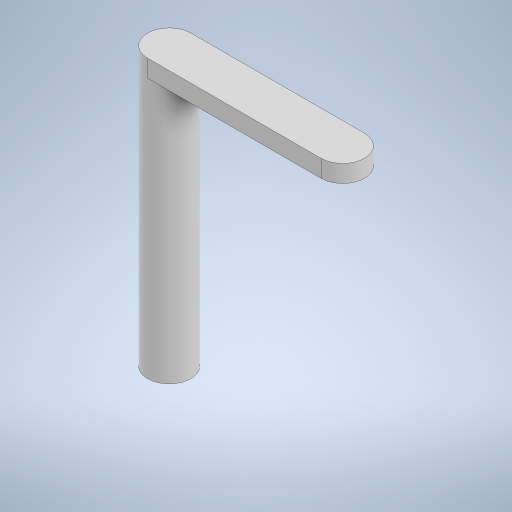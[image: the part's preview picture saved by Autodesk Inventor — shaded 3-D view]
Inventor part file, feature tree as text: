
AUTODESK INVENTOR PART (.ipt)
format: ipt  version: 2024 (Build 280153000, 153)  size: 237,568 bytes
history: native  units: in
note: dims shown in document units (in); Inventor stores cm internally (conversion verified against a paired STEP export)
features: extrude x2, sketch x2
ambient origin geometry x8: Origin, YZ Plane, XZ Plane, XY Plane, X Axis, Y Axis, Z Axis, Center Point
bodies: Solid1 (feature_tree)
feature tree (4):
  extrude  "Extrusion1"  Depth=3.0in TaperAngle=0.0deg
  extrude  "Extrusion2"  Depth=0.2in TaperAngle=0.0deg
  sketch  "Sketch1"  dims[d0=0.5in d1=3.0in d2=0.0in]
  sketch  "Sketch2"  dims[d4=0.25in d7=0.2in d8=0.0in d10=2.0in d11=0.25in d12=2.0in d13=0.25in]
